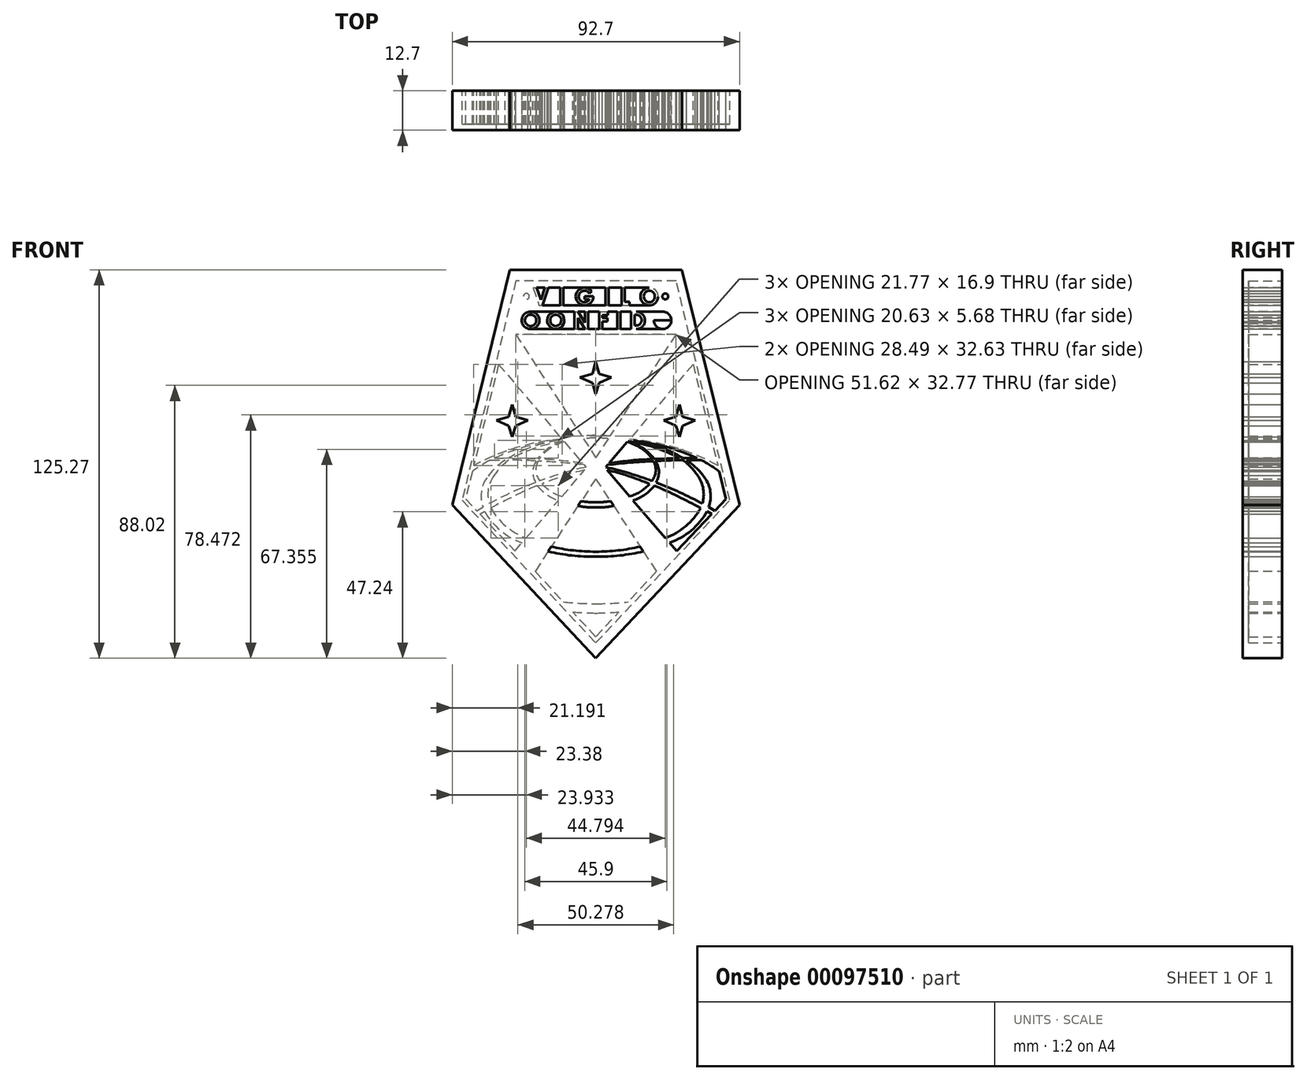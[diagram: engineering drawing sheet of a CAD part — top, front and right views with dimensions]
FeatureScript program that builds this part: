
annotation { "Feature Type Name" : "Feature", "Feature Type Description" : "" }
export const myFeature = defineFeature(function(context is Context, id is Id, definition is map)
    precondition{}
    {
        {
            var Q0;
            Q0=qCreatedBy(makeId("Front.planeOp"),FACE);
            var sketch = newSketch(context, id + "F0", { "sketchPlane" : qUnion([Q0])});
            skLineSegment(sketch, "E0", {"start": v(-27.72, 63.66) * mm, "end": v(27.8, 63.66) * mm});
            skLineSegment(sketch, "E1", {"start": v(27.8, 63.66) * mm, "end": v(46.37, -12.24) * mm});
            skLineSegment(sketch, "E2", {"start": v(46.37, -12.24) * mm, "end": v(0, -61.61) * mm});
            skLineSegment(sketch, "E3", {"start": v(0, -61.61) * mm, "end": v(-46.33, -12.22) * mm});
            skLineSegment(sketch, "E4", {"start": v(-46.33, -12.22) * mm, "end": v(-27.72, 63.66) * mm});
            skLineSegment(sketch, "E5", {"start": v(0, -56.69) * mm, "end": v(43.22, -10.66) * mm});
            skLineSegment(sketch, "E6", {"start": v(43.22, -10.66) * mm, "end": v(25.91, 60.08) * mm});
            skLineSegment(sketch, "E7", {"start": v(25.91, 60.08) * mm, "end": v(-25.8, 60.08) * mm});
            skLineSegment(sketch, "E8", {"start": v(-25.8, 60.08) * mm, "end": v(-43.16, -10.68) * mm});
            skLineSegment(sketch, "E9", {"start": v(-43.16, -10.68) * mm, "end": v(0, -56.69) * mm});
            skLineSegment(sketch, "E10", {"start": v(0, 42.8) * mm, "end": v(-25.81, 42.8) * mm});
            skLineSegment(sketch, "E11", {"start": v(-25.81, 42.8) * mm, "end": v(-4.52, 10.03) * mm});
            skArc(sketch, "E12", {"start": v(0, 10.25) * mm, "mid": v(-2.26, 10.2) * mm, "end": v(-4.52, 10.03) * mm});
            skArc(sketch, "E13", {"start": v(0, 9.4) * mm, "mid": v(-2, 9.35) * mm, "end": v(-3.98, 9.2) * mm});
            skLineSegment(sketch, "E14", {"start": v(-3.98, 9.2) * mm, "end": v(0, 3.07) * mm});
            skLineSegment(sketch, "E15", {"start": v(-31.38, 33.18) * mm, "end": v(-39.38, 0.55) * mm});
            skLineSegment(sketch, "E16", {"start": v(-39.38, 0.55) * mm, "end": v(-42.02, -10.21) * mm});
            skLineSegment(sketch, "E17", {"start": v(-42.02, -10.21) * mm, "end": v(-38.44, -14.03) * mm});
            skLineSegment(sketch, "E18", {"start": v(-38.44, -14.03) * mm, "end": v(-36.41, -12.8) * mm});
            skLineSegment(sketch, "E19", {"start": v(0, -3.74) * mm, "end": v(-4.71, -10.93) * mm});
            skArc(sketch, "E20", {"start": v(-4.71, -10.93) * mm, "mid": v(-2.37, -11.25) * mm, "end": v(0, -11.33) * mm});
            skLineSegment(sketch, "E21", {"start": v(-31.38, 33.18) * mm, "end": v(-10.9, 9.05) * mm});
            skArc(sketch, "E22", {"start": v(-10.9, 9.05) * mm, "mid": v(-25.59, 6.3) * mm, "end": v(-39.38, 0.55) * mm});
            skLineSegment(sketch, "E23", {"start": v(-4.71, -10.93) * mm, "end": v(-19.6, -33.58) * mm});
            skArc(sketch, "E24", {"start": v(-5.74, -12.49) * mm, "mid": v(-2.88, -12.9) * mm, "end": v(0, -12.98) * mm});
            skArc(sketch, "E25", {"start": v(-14.35, -25.6) * mm, "mid": v(-7.22, -26.85) * mm, "end": v(0, -27.25) * mm});
            skArc(sketch, "E26", {"start": v(-15.37, -27.15) * mm, "mid": v(-7.74, -28.5) * mm, "end": v(0, -28.86) * mm});
            skLineSegment(sketch, "E27", {"start": v(-19.6, -33.58) * mm, "end": v(-10.47, -43.42) * mm});
            skArc(sketch, "E28", {"start": v(-10.47, -43.42) * mm, "mid": v(-5.24, -43.89) * mm, "end": v(0, -44) * mm});
            skLineSegment(sketch, "E29", {"start": v(0, -54.67) * mm, "end": v(-7.47, -46.7) * mm});
            skArc(sketch, "E30", {"start": v(-7.47, -46.7) * mm, "mid": v(-3.74, -46.95) * mm, "end": v(0, -47.05) * mm});
            skLineSegment(sketch, "E31", {"start": v(-37.35, -15.14) * mm, "end": v(-26.15, -27.08) * mm});
            skLineSegment(sketch, "E32", {"start": v(-26.15, -27.08) * mm, "end": v(-3.6, -0.9) * mm});
            skLineSegment(sketch, "E33", {"start": v(-37.35, -15.14) * mm, "end": v(-35.92, -14.27) * mm});
            skArc(sketch, "E34", {"start": v(-35.92, -14.27) * mm, "mid": v(-30.77, -20.4) * mm, "end": v(-23.8, -24.36) * mm});
            skArc(sketch, "E35", {"start": v(-33.83, -13.18) * mm, "mid": v(-29, -19) * mm, "end": v(-22.48, -22.82) * mm});
            skArc(sketch, "E36", {"start": v(-18.92, -5.92) * mm, "mid": v(-26.46, -9.38) * mm, "end": v(-33.83, -13.18) * mm});
            skArc(sketch, "E37", {"start": v(-18.92, -5.92) * mm, "mid": v(-15.85, -8.84) * mm, "end": v(-12.07, -10.73) * mm});
            skArc(sketch, "E38", {"start": v(-17.38, -5.41) * mm, "mid": v(-14.42, -7.83) * mm, "end": v(-10.96, -9.45) * mm});
            skArc(sketch, "E39", {"start": v(-3.6, -0.9) * mm, "mid": v(-10.58, -2.87) * mm, "end": v(-17.38, -5.41) * mm});
            skArc(sketch, "E40", {"start": v(-35.16, -3.42) * mm, "mid": v(-36.94, -7.95) * mm, "end": v(-36.41, -12.8) * mm});
            skArc(sketch, "E41", {"start": v(-29.26, 2.3) * mm, "mid": v(-32.47, -0.3) * mm, "end": v(-35.16, -3.42) * mm});
            skArc(sketch, "E42", {"start": v(-34.08, 2.3) * mm, "mid": v(-37.02, 0.55) * mm, "end": v(-39.85, -1.36) * mm});
            skLineSegment(sketch, "E43", {"start": v(-34.08, 2.3) * mm, "end": v(-29.26, 2.3) * mm});
            skArc(sketch, "E44", {"start": v(-19.45, -4.9) * mm, "mid": v(-27.02, -8.1) * mm, "end": v(-34.4, -11.72) * mm});
            skArc(sketch, "E45", {"start": v(-3.2, 0) * mm, "mid": v(-10.74, -1.94) * mm, "end": v(-18.12, -4.43) * mm});
            skArc(sketch, "E46", {"start": v(-18.7, 1.96) * mm, "mid": v(-19.32, -1.32) * mm, "end": v(-18.12, -4.43) * mm});
            skArc(sketch, "E47", {"start": v(-32.86, -2.67) * mm, "mid": v(-34.67, -7.02) * mm, "end": v(-34.4, -11.72) * mm});
            skArc(sketch, "E48", {"start": v(-28.11, 2.3) * mm, "mid": v(-30.69, 0) * mm, "end": v(-32.86, -2.67) * mm});
            skArc(sketch, "E49", {"start": v(-19.27, 1.97) * mm, "mid": v(-23.69, 2.2) * mm, "end": v(-28.11, 2.3) * mm});
            skArc(sketch, "E50", {"start": v(-19.27, 1.97) * mm, "mid": v(-20.35, -1.44) * mm, "end": v(-19.45, -4.9) * mm});
            skArc(sketch, "E51", {"start": v(-3.77, 0.73) * mm, "mid": v(-11.22, 1.5) * mm, "end": v(-18.7, 1.96) * mm});
            skLineSegment(sketch, "E52", {"start": v(-3.77, 0.73) * mm, "end": v(-3.2, 0) * mm});
            skArc(sketch, "E53", {"start": v(-12.08, 8.58) * mm, "mid": v(-22.62, 6.57) * mm, "end": v(-32.71, 2.94) * mm});
            skArc(sketch, "E54", {"start": v(-12.08, 8.58) * mm, "mid": v(-17.09, 7.52) * mm, "end": v(-21.97, 6) * mm});
            skArc(sketch, "E55", {"start": v(-21.97, 6) * mm, "mid": v(-25.12, 4.62) * mm, "end": v(-28.11, 2.9) * mm});
            skLineSegment(sketch, "E56", {"start": v(-32.71, 2.94) * mm, "end": v(-28.11, 2.9) * mm});
            skLineSegment(sketch, "E57", {"start": v(-27.03, 2.9) * mm, "end": v(-18.91, 2.62) * mm});
            skArc(sketch, "E58", {"start": v(-10.43, 8.4) * mm, "mid": v(-18.97, 6.36) * mm, "end": v(-27.03, 2.9) * mm});
            skArc(sketch, "E59", {"start": v(-10.43, 8.4) * mm, "mid": v(-15.12, 6.17) * mm, "end": v(-18.91, 2.62) * mm});
            skArc(sketch, "E60", {"start": v(-4.3, 1.24) * mm, "mid": v(-11.3, 2.15) * mm, "end": v(-18.33, 2.58) * mm});
            skArc(sketch, "E61", {"start": v(-10.15, 8.17) * mm, "mid": v(-14.7, 6.06) * mm, "end": v(-18.33, 2.58) * mm});
            skLineSegment(sketch, "E62", {"start": v(-10.15, 8.17) * mm, "end": v(-4.3, 1.24) * mm});
            skLineSegment(sketch, "E63", {"start": v(-26.95, 21.38) * mm, "end": v(-26.95, 9.07) * mm});
            skLineSegment(sketch, "E64", {"start": v(-33.32, 15.14) * mm, "end": v(-20.5, 15.14) * mm});
            skPoint(sketch, "E65", {"position": v(-26.95, 15.14) * mm});
            skPoint(sketch, "E66", {"position": v(-26.95, 20.22) * mm});
            skPoint(sketch, "E67", {"position": v(-21.87, 15.14) * mm});
            skPoint(sketch, "E68", {"position": v(-26.95, 9.8) * mm});
            skPoint(sketch, "E69", {"position": v(-32.03, 15.14) * mm});
            skLineSegment(sketch, "E70", {"start": v(-26.95, 9.8) * mm, "end": v(-28.06, 13.3) * mm});
            skLineSegment(sketch, "E71", {"start": v(-28.06, 13.3) * mm, "end": v(-32.03, 15.14) * mm});
            skLineSegment(sketch, "E72", {"start": v(-32.03, 15.14) * mm, "end": v(-28.06, 16.24) * mm});
            skLineSegment(sketch, "E73", {"start": v(-28.06, 16.24) * mm, "end": v(-26.95, 20.22) * mm});
            skLineSegment(sketch, "E74", {"start": v(-26.95, 20.22) * mm, "end": v(-25.85, 16.26) * mm});
            skLineSegment(sketch, "E75", {"start": v(-25.85, 16.26) * mm, "end": v(-21.87, 15.14) * mm});
            skLineSegment(sketch, "E76", {"start": v(-21.87, 15.14) * mm, "end": v(-25.85, 13.31) * mm});
            skLineSegment(sketch, "E77", {"start": v(-25.85, 13.31) * mm, "end": v(-26.95, 9.8) * mm});
            skLineSegment(sketch, "E78", {"start": v(-5.4, 28.93) * mm, "end": v(6.92, 28.93) * mm});
            skLineSegment(sketch, "E79", {"start": v(0, 35.2) * mm, "end": v(0, 22.48) * mm});
            skPoint(sketch, "E80", {"position": v(-5.08, 28.93) * mm});
            skPoint(sketch, "E81", {"position": v(0, 34) * mm});
            skPoint(sketch, "E82", {"position": v(0, 23.6) * mm});
            skLineSegment(sketch, "E83", {"start": v(-5.08, 28.93) * mm, "end": v(-1.1, 27.16) * mm});
            skLineSegment(sketch, "E84", {"start": v(-1.1, 27.16) * mm, "end": v(0, 23.6) * mm});
            skLineSegment(sketch, "E85", {"start": v(-5.08, 28.93) * mm, "end": v(-1.1, 30.07) * mm});
            skLineSegment(sketch, "E86", {"start": v(-1.1, 30.07) * mm, "end": v(0, 34) * mm});
            skLineSegment(sketch, "E87.MirrorCS", {"start": v(1.1, 30.07) * mm, "end": v(0, 34) * mm});
            skLineSegment(sketch, "E88.MirrorCS", {"start": v(5.08, 28.93) * mm, "end": v(1.1, 30.07) * mm});
            skLineSegment(sketch, "E89.MirrorCS", {"start": v(5.08, 28.93) * mm, "end": v(1.1, 27.16) * mm});
            skLineSegment(sketch, "E90.MirrorCS", {"start": v(1.1, 27.16) * mm, "end": v(0, 23.6) * mm});
            skLineSegment(sketch, "E91.MirrorCS", {"start": v(25.81, 42.8) * mm, "end": v(4.52, 10.03) * mm});
            skLineSegment(sketch, "E92.MirrorCS", {"start": v(0, 42.8) * mm, "end": v(25.81, 42.8) * mm});
            skLineSegment(sketch, "E93.MirrorCS", {"start": v(26.95, 20.22) * mm, "end": v(25.85, 16.26) * mm});
            skLineSegment(sketch, "E94.MirrorCS", {"start": v(28.06, 16.24) * mm, "end": v(26.95, 20.22) * mm});
            skLineSegment(sketch, "E95.MirrorCS", {"start": v(32.03, 15.14) * mm, "end": v(28.06, 16.24) * mm});
            skLineSegment(sketch, "E96.MirrorCS", {"start": v(28.06, 13.3) * mm, "end": v(32.03, 15.14) * mm});
            skLineSegment(sketch, "E97.MirrorCS", {"start": v(26.95, 9.8) * mm, "end": v(28.06, 13.3) * mm});
            skLineSegment(sketch, "E98.MirrorCS", {"start": v(25.85, 13.31) * mm, "end": v(26.95, 9.8) * mm});
            skLineSegment(sketch, "E99.MirrorCS", {"start": v(21.87, 15.14) * mm, "end": v(25.85, 13.31) * mm});
            skLineSegment(sketch, "E100.MirrorCS", {"start": v(25.85, 16.26) * mm, "end": v(21.87, 15.14) * mm});
            skLineSegment(sketch, "E101.MirrorCS", {"start": v(31.38, 33.18) * mm, "end": v(10.9, 9.05) * mm});
            skLineSegment(sketch, "E102.MirrorCS", {"start": v(31.38, 33.18) * mm, "end": v(39.38, 0.55) * mm});
            skArc(sketch, "E103.MirrorCS", {"start": v(10.9, 9.05) * mm, "mid": v(25.59, 6.3) * mm, "end": v(39.38, 0.55) * mm});
            skArc(sketch, "E104.MirrorCS", {"start": v(12.08, 8.58) * mm, "mid": v(22.62, 6.57) * mm, "end": v(32.71, 2.94) * mm});
            skArc(sketch, "E105.MirrorCS", {"start": v(10.43, 8.4) * mm, "mid": v(18.97, 6.36) * mm, "end": v(27.03, 2.9) * mm});
            skArc(sketch, "E106.MirrorCS", {"start": v(21.97, 6) * mm, "mid": v(25.12, 4.62) * mm, "end": v(28.11, 2.9) * mm});
            skArc(sketch, "E107.MirrorCS", {"start": v(12.08, 8.58) * mm, "mid": v(17.09, 7.52) * mm, "end": v(21.97, 6) * mm});
            skLineSegment(sketch, "E108.MirrorCS", {"start": v(32.71, 2.94) * mm, "end": v(28.11, 2.9) * mm});
            skArc(sketch, "E109.MirrorCS", {"start": v(29.26, 2.3) * mm, "mid": v(32.47, -0.3) * mm, "end": v(35.16, -3.42) * mm});
            skArc(sketch, "E110.MirrorCS", {"start": v(34.08, 2.3) * mm, "mid": v(37.02, 0.55) * mm, "end": v(39.85, -1.36) * mm});
            skLineSegment(sketch, "E111.MirrorCS", {"start": v(39.38, 0.55) * mm, "end": v(42.02, -10.21) * mm});
            skLineSegment(sketch, "E112.MirrorCS", {"start": v(42.02, -10.21) * mm, "end": v(38.44, -14.03) * mm});
            skLineSegment(sketch, "E113.MirrorCS", {"start": v(38.44, -14.03) * mm, "end": v(36.41, -12.8) * mm});
            skArc(sketch, "E114.MirrorCS", {"start": v(35.16, -3.42) * mm, "mid": v(36.94, -7.95) * mm, "end": v(36.41, -12.8) * mm});
            skArc(sketch, "E115.MirrorCS", {"start": v(32.86, -2.67) * mm, "mid": v(34.67, -7.02) * mm, "end": v(34.4, -11.72) * mm});
            skArc(sketch, "E116.MirrorCS", {"start": v(28.11, 2.3) * mm, "mid": v(30.69, 0) * mm, "end": v(32.86, -2.67) * mm});
            skArc(sketch, "E117.MirrorCS", {"start": v(19.27, 1.97) * mm, "mid": v(23.69, 2.2) * mm, "end": v(28.11, 2.3) * mm});
            skLineSegment(sketch, "E118.MirrorCS", {"start": v(27.03, 2.9) * mm, "end": v(18.91, 2.62) * mm});
            skArc(sketch, "E119.MirrorCS", {"start": v(10.43, 8.4) * mm, "mid": v(15.12, 6.17) * mm, "end": v(18.91, 2.62) * mm});
            skArc(sketch, "E120.MirrorCS", {"start": v(10.15, 8.17) * mm, "mid": v(14.7, 6.06) * mm, "end": v(18.33, 2.58) * mm});
            skArc(sketch, "E121.MirrorCS", {"start": v(4.3, 1.24) * mm, "mid": v(11.3, 2.15) * mm, "end": v(18.33, 2.58) * mm});
            skLineSegment(sketch, "E122.MirrorCS", {"start": v(10.15, 8.17) * mm, "end": v(4.3, 1.24) * mm});
            skArc(sketch, "E123.MirrorCS", {"start": v(3.77, 0.73) * mm, "mid": v(11.22, 1.5) * mm, "end": v(18.7, 1.96) * mm});
            skArc(sketch, "E124.MirrorCS", {"start": v(3.2, 0) * mm, "mid": v(10.74, -1.94) * mm, "end": v(18.12, -4.43) * mm});
            skArc(sketch, "E125.MirrorCS", {"start": v(18.7, 1.96) * mm, "mid": v(19.32, -1.32) * mm, "end": v(18.12, -4.43) * mm});
            skArc(sketch, "E126.MirrorCS", {"start": v(19.27, 1.97) * mm, "mid": v(20.35, -1.44) * mm, "end": v(19.45, -4.9) * mm});
            skArc(sketch, "E127.MirrorCS", {"start": v(19.45, -4.9) * mm, "mid": v(27.02, -8.1) * mm, "end": v(34.4, -11.72) * mm});
            skArc(sketch, "E128.MirrorCS", {"start": v(5.74, -12.49) * mm, "mid": v(2.88, -12.9) * mm, "end": v(0, -12.98) * mm});
            skArc(sketch, "E129.MirrorCS", {"start": v(4.71, -10.93) * mm, "mid": v(2.37, -11.25) * mm, "end": v(0, -11.33) * mm});
            skLineSegment(sketch, "E130.MirrorCS", {"start": v(0, -3.74) * mm, "end": v(4.71, -10.93) * mm});
            skArc(sketch, "E131.MirrorCS", {"start": v(14.35, -25.6) * mm, "mid": v(7.22, -26.85) * mm, "end": v(0, -27.25) * mm});
            skLineSegment(sketch, "E132.MirrorCS", {"start": v(4.71, -10.93) * mm, "end": v(19.6, -33.58) * mm});
            skArc(sketch, "E133.MirrorCS", {"start": v(15.37, -27.15) * mm, "mid": v(7.74, -28.5) * mm, "end": v(0, -28.86) * mm});
            skArc(sketch, "E134.MirrorCS", {"start": v(10.47, -43.42) * mm, "mid": v(5.24, -43.89) * mm, "end": v(0, -44) * mm});
            skLineSegment(sketch, "E135.MirrorCS", {"start": v(19.6, -33.58) * mm, "end": v(10.47, -43.42) * mm});
            skArc(sketch, "E136.MirrorCS", {"start": v(7.47, -46.7) * mm, "mid": v(3.74, -46.95) * mm, "end": v(0, -47.05) * mm});
            skLineSegment(sketch, "E137.MirrorCS", {"start": v(0, -54.67) * mm, "end": v(7.47, -46.7) * mm});
            skArc(sketch, "E138.MirrorCS", {"start": v(0, 9.4) * mm, "mid": v(2, 9.35) * mm, "end": v(3.98, 9.2) * mm});
            skLineSegment(sketch, "E139.MirrorCS", {"start": v(3.98, 9.2) * mm, "end": v(0, 3.07) * mm});
            skArc(sketch, "E140.MirrorCS", {"start": v(0, 10.25) * mm, "mid": v(2.26, 10.2) * mm, "end": v(4.52, 10.03) * mm});
            skLineSegment(sketch, "E141", {"start": v(-21, 57.88) * mm, "end": v(22.36, 57.88) * mm});
            skLineSegment(sketch, "E142", {"start": v(-20.05, 52.23) * mm, "end": v(23.28, 52.23) * mm});
            skLineSegment(sketch, "E143", {"start": v(-24.15, 50.19) * mm, "end": v(26.1, 50.19) * mm});
            skLineSegment(sketch, "E144", {"start": v(-24.97, 44.55) * mm, "end": v(26.4, 44.55) * mm});
            skLineSegment(sketch, "E145", {"start": v(-20.24, 57.88) * mm, "end": v(-18.3, 52.23) * mm});
            skLineSegment(sketch, "E146", {"start": v(-19.09, 57.88) * mm, "end": v(-17.76, 54.01) * mm});
            skLineSegment(sketch, "E147", {"start": v(-17.76, 54.01) * mm, "end": v(-16.44, 57.88) * mm});
            skLineSegment(sketch, "E148", {"start": v(-15.29, 57.88) * mm, "end": v(-17.2, 52.23) * mm});
            skLineSegment(sketch, "E149", {"start": v(-11.48, 57.88) * mm, "end": v(-11.48, 52.23) * mm});
            skLineSegment(sketch, "E150", {"start": v(-10.43, 57.88) * mm, "end": v(-10.43, 52.23) * mm});
            skLineSegment(sketch, "E151", {"start": v(3.05, 57.88) * mm, "end": v(3.05, 52.23) * mm});
            skLineSegment(sketch, "E152", {"start": v(4.15, 57.88) * mm, "end": v(4.15, 52.23) * mm});
            skLineSegment(sketch, "E153", {"start": v(8.3, 57.88) * mm, "end": v(8.3, 52.23) * mm});
            skLineSegment(sketch, "E154", {"start": v(10.92, 52.23) * mm, "end": v(10.92, 53.33) * mm});
            skLineSegment(sketch, "E155", {"start": v(10.92, 53.33) * mm, "end": v(9.39, 53.33) * mm});
            skLineSegment(sketch, "E156", {"start": v(9.39, 53.33) * mm, "end": v(9.39, 57.88) * mm});
            skLineSegment(sketch, "E157", {"start": v(-23.92, 55.08) * mm, "end": v(-20.8, 55.08) * mm});
            skLineSegment(sketch, "E158", {"start": v(-22.42, 54.08) * mm, "end": v(-22.42, 56.2) * mm});
            skCircle(sketch, "E159", {"center": v(-22.42, 55.08) * mm, "radius": 0.95 * mm});
            skCircle(sketch, "E160.MirrorC", {"center": v(22.42, 55.08) * mm, "radius": 0.95 * mm});
            skLineSegment(sketch, "E161", {"start": v(1.04, 50.19) * mm, "end": v(1.04, 44.55) * mm});
            skLineSegment(sketch, "E162", {"start": v(3.87, 50.19) * mm, "end": v(3.87, 49.1) * mm});
            skLineSegment(sketch, "E163", {"start": v(3.87, 49.1) * mm, "end": v(2.13, 49.1) * mm});
            skLineSegment(sketch, "E164", {"start": v(2.13, 49.1) * mm, "end": v(2.13, 48.15) * mm});
            skLineSegment(sketch, "E165", {"start": v(2.13, 48.15) * mm, "end": v(3.74, 48.15) * mm});
            skLineSegment(sketch, "E166", {"start": v(3.74, 48.15) * mm, "end": v(3.74, 47.06) * mm});
            skLineSegment(sketch, "E167", {"start": v(3.74, 47.06) * mm, "end": v(2.13, 47.06) * mm});
            skLineSegment(sketch, "E168", {"start": v(2.13, 47.06) * mm, "end": v(2.13, 44.55) * mm});
            skLineSegment(sketch, "E169", {"start": v(6.88, 50.19) * mm, "end": v(6.88, 44.55) * mm});
            skLineSegment(sketch, "E170", {"start": v(7.98, 50.19) * mm, "end": v(7.98, 44.55) * mm});
            skLineSegment(sketch, "E171", {"start": v(11.37, 50.19) * mm, "end": v(11.37, 44.55) * mm});
            skLineSegment(sketch, "E172", {"start": v(-6.9, 50.19) * mm, "end": v(-6.9, 44.55) * mm});
            skLineSegment(sketch, "E173", {"start": v(-2.44, 50.19) * mm, "end": v(-2.44, 44.55) * mm});
            skLineSegment(sketch, "E174", {"start": v(-3.53, 50.19) * mm, "end": v(-3.53, 46.59) * mm});
            skLineSegment(sketch, "E175", {"start": v(-3.53, 46.59) * mm, "end": v(-5.8, 50.19) * mm});
            skLineSegment(sketch, "E176", {"start": v(-5.8, 44.55) * mm, "end": v(-5.8, 48.14) * mm});
            skLineSegment(sketch, "E177", {"start": v(-5.8, 48.14) * mm, "end": v(-3.53, 44.55) * mm});
            skLineSegment(sketch, "E178", {"start": v(21.54, 50.19) * mm, "end": v(21.54, 44.55) * mm});
            skLineSegment(sketch, "E179", {"start": v(17.82, 47.41) * mm, "end": v(25.25, 47.41) * mm});
            skEllipse(sketch, "E180", {"center": v(21.54, 47.37) * mm, "majorRadius": 2.82 * mm, "minorRadius": 2.81 * mm, "majorAxis": v(0, -1)});
            skEllipse(sketch, "E181", {"center": v(21.54, 47.37) * mm, "majorRadius": 1.85 * mm, "minorRadius": 1.8 * mm, "majorAxis": v(0, -1)});
            skLineSegment(sketch, "E182", {"start": v(17.26, 57.88) * mm, "end": v(17.26, 52.23) * mm});
            skLineSegment(sketch, "E183", {"start": v(13.99, 55.05) * mm, "end": v(20.7, 55.05) * mm});
            skPoint(sketch, "E183.startSnap0", {"position": v(17.26, 55.05) * mm});
            skEllipse(sketch, "E184", {"center": v(17.26, 55.05) * mm, "majorRadius": 2.82 * mm, "minorRadius": 2.87 * mm, "majorAxis": v(0, -1)});
            skEllipse(sketch, "E185", {"center": v(17.26, 55.05) * mm, "majorRadius": 1.84 * mm, "minorRadius": 1.78 * mm, "majorAxis": v(0, -1)});
            skLineSegment(sketch, "E186", {"start": v(-12.94, 50.19) * mm, "end": v(-12.94, 44.55) * mm});
            skEllipse(sketch, "E187", {"center": v(-12.94, 47.37) * mm, "majorRadius": 2.82 * mm, "minorRadius": 2.8 * mm, "majorAxis": v(0, -1)});
            skEllipse(sketch, "E188", {"center": v(-12.94, 47.37) * mm, "majorRadius": 1.83 * mm, "minorRadius": 1.78 * mm, "majorAxis": v(0, -1)});
            skLineSegment(sketch, "E189", {"start": v(-21.03, 50.19) * mm, "end": v(-21.03, 44.55) * mm});
            skEllipse(sketch, "E190", {"center": v(-21.03, 47.37) * mm, "majorRadius": 2.82 * mm, "minorRadius": 2.88 * mm, "majorAxis": v(0, -1)});
            skEllipse(sketch, "E191", {"center": v(-21.03, 47.37) * mm, "majorRadius": 1.85 * mm, "minorRadius": 1.85 * mm, "majorAxis": v(0, -1)});
            skLineSegment(sketch, "E192", {"start": v(-18.75, 49.08) * mm, "end": v(-22.09, 45.84) * mm});
            skLineSegment(sketch, "E193", {"start": v(-18.74, 45.66) * mm, "end": v(-19.45, 46.4) * mm});
            skLineSegment(sketch, "E194", {"start": v(11.37, 50.19) * mm, "end": v(13.06, 50.19) * mm});
            skArc(sketch, "E195", {"start": v(13.06, 50.19) * mm, "mid": v(15.88, 47.37) * mm, "end": v(13.06, 44.55) * mm});
            skLineSegment(sketch, "E196", {"start": v(12.46, 49.14) * mm, "end": v(12.46, 45.7) * mm});
            skLineSegment(sketch, "E197", {"start": v(12.46, 49.14) * mm, "end": v(13.06, 49.14) * mm});
            skLineSegment(sketch, "E198", {"start": v(12.46, 45.7) * mm, "end": v(13.06, 45.7) * mm});
            skArc(sketch, "E199", {"start": v(13.06, 45.7) * mm, "mid": v(14.77, 47.42) * mm, "end": v(13.06, 49.14) * mm});
            skLineSegment(sketch, "E200", {"start": v(-3.64, 57.88) * mm, "end": v(-3.64, 52.23) * mm});
            skEllipse(sketch, "E201", {"center": v(-3.64, 55.05) * mm, "majorRadius": 2.82 * mm, "minorRadius": 2.86 * mm, "majorAxis": v(0, -1)});
            skEllipse(sketch, "E202", {"center": v(-3.64, 55.05) * mm, "majorRadius": 1.85 * mm, "minorRadius": 1.85 * mm, "majorAxis": v(0, -1)});
            skLineSegment(sketch, "E203", {"start": v(-4.7, 53.53) * mm, "end": v(-1.38, 56.78) * mm});
            skLineSegment(sketch, "E204", {"start": v(-0.78, 55.13) * mm, "end": v(-3.64, 55.13) * mm});
            skLineSegment(sketch, "E205", {"start": v(-3.64, 55.13) * mm, "end": v(-3.64, 54.12) * mm});
            skLineSegment(sketch, "E206", {"start": v(-3.64, 54.12) * mm, "end": v(-2.04, 54.12) * mm});
            skLineSegment(sketch, "E207", {"start": v(2.13, 47.06) * mm, "end": v(2.13, 48.15) * mm});
            skLineSegment(sketch, "E208.MirrorCS", {"start": v(26.15, -27.08) * mm, "end": v(3.6, -0.9) * mm});
            skArc(sketch, "E209.MirrorCS", {"start": v(3.6, -0.9) * mm, "mid": v(10.58, -2.87) * mm, "end": v(17.38, -5.41) * mm});
            skArc(sketch, "E210.MirrorCS", {"start": v(17.38, -5.41) * mm, "mid": v(14.42, -7.83) * mm, "end": v(10.96, -9.45) * mm});
            skArc(sketch, "E211.MirrorCS", {"start": v(18.92, -5.92) * mm, "mid": v(15.85, -8.84) * mm, "end": v(12.07, -10.73) * mm});
            skArc(sketch, "E212.MirrorCS", {"start": v(18.92, -5.92) * mm, "mid": v(26.46, -9.38) * mm, "end": v(33.83, -13.18) * mm});
            skArc(sketch, "E213.MirrorCS", {"start": v(33.83, -13.18) * mm, "mid": v(29, -19) * mm, "end": v(22.48, -22.82) * mm});
            skArc(sketch, "E214.MirrorCS", {"start": v(35.92, -14.27) * mm, "mid": v(30.77, -20.4) * mm, "end": v(23.8, -24.36) * mm});
            skLineSegment(sketch, "E215.MirrorCS", {"start": v(37.35, -15.14) * mm, "end": v(26.15, -27.08) * mm});
            skLineSegment(sketch, "E216.MirrorCS", {"start": v(37.35, -15.14) * mm, "end": v(35.92, -14.27) * mm});
            skLineSegment(sketch, "E217", {"start": v(3.77, 0.73) * mm, "end": v(3.2, 0) * mm});
            skLineSegment(sketch, "E218.MirrorCS", {"start": v(34.08, 2.3) * mm, "end": v(29.26, 2.3) * mm});
            skSolve(sketch);
        }
        {
            var Q0;
            Q0=makeQuery(id+"F0.imprint","IMPRINT",FACE,{"disambiguationData":[TD([[makeQuery(id+"F0.imprint","IMPRINT",EDGE,{"derivedFrom":sQuery(id+"F0.wireOp",EDGE,"E0")}),-1.0]])]});
            var Q1;
            Q1=makeQuery(id+"F0.imprint","IMPRINT",FACE,{"disambiguationData":[TD([[makeQuery(id+"F0.imprint","IMPRINT",EDGE,{"derivedFrom":sQuery(id+"F0.wireOp",EDGE,"E15")}),1.0]])]});
            var Q2;
            Q2=makeQuery(id+"F0.imprint","IMPRINT",FACE,{"disambiguationData":[TD([[makeQuery(id+"F0.imprint","IMPRINT",EDGE,{"derivedFrom":sQuery(id+"F0.wireOp",EDGE,"E53")}),1.0]])]});
            var Q3;
            {var subQ0=sQuery(id+"F0.wireOp",EDGE,"E17");Q3=makeQuery(id+"F0.imprint","IMPRINT",FACE,{"disambiguationData":[TD([[makeQuery(id+"F0.imprint","IMPRINT",EDGE,{"derivedFrom":subQ0}),1.0]])]});}
            var Q4;
            Q4=makeQuery(id+"F0.imprint","IMPRINT",FACE,{"disambiguationData":[TD([[makeQuery(id+"F0.imprint","IMPRINT",EDGE,{"derivedFrom":sQuery(id+"F0.wireOp",EDGE,"E44")}),-1.0]])]});
            var Q5;
            Q5=makeQuery(id+"F0.imprint","IMPRINT",FACE,{"disambiguationData":[TD([[makeQuery(id+"F0.imprint","IMPRINT",EDGE,{"derivedFrom":sQuery(id+"F0.wireOp",EDGE,"E57")}),1.0]])]});
            var Q6;
            Q6=makeQuery(id+"F0.imprint","IMPRINT",FACE,{"disambiguationData":[TD([[makeQuery(id+"F0.imprint","IMPRINT",EDGE,{"derivedFrom":sQuery(id+"F0.wireOp",EDGE,"E60")}),-1.0]])]});
            var Q7;
            Q7=makeQuery(id+"F0.imprint","IMPRINT",FACE,{"disambiguationData":[TD([[makeQuery(id+"F0.imprint","IMPRINT",EDGE,{"derivedFrom":sQuery(id+"F0.wireOp",EDGE,"E45")}),-1.0]])]});
            var Q8;
            {var subQ2=sQuery(id+"F0.wireOp",EDGE,"E38");Q8=makeQuery(id+"F0.imprint","IMPRINT",FACE,{"disambiguationData":[TD([[makeQuery(id+"F0.imprint","IMPRINT",EDGE,{"derivedFrom":subQ2}),1.0]])]});}
            var Q9;
            {var subQ0=sQuery(id+"F0.wireOp",EDGE,"E35");Q9=makeQuery(id+"F0.imprint","IMPRINT",FACE,{"disambiguationData":[TD([[makeQuery(id+"F0.imprint","IMPRINT",EDGE,{"derivedFrom":subQ0}),1.0]])]});}
            var Q10;
            {var subQ0=sQuery(id+"F0.wireOp",EDGE,"E31");Q10=makeQuery(id+"F0.imprint","IMPRINT",FACE,{"disambiguationData":[TD([[makeQuery(id+"F0.imprint","IMPRINT",EDGE,{"derivedFrom":subQ0}),1.0]])]});}
            var Q11;
            {var subQ1=sQuery(id+"F0.wireOp",EDGE,"E24");Q11=makeQuery(id+"F0.imprint","IMPRINT",FACE,{"disambiguationData":[TD([[makeQuery(id+"F0.imprint","IMPRINT",EDGE,{"derivedFrom":subQ1}),-1.0]])]});}
            var Q12;
            Q12=makeQuery(id+"F0.imprint","IMPRINT",FACE,{"disambiguationData":[TD([[makeQuery(id+"F0.imprint","IMPRINT",EDGE,{"derivedFrom":sQuery(id+"F0.wireOp",EDGE,"E19")}),1.0]])]});
            var Q13;
            {var subQ1=sQuery(id+"F0.wireOp",EDGE,"E26");Q13=makeQuery(id+"F0.imprint","IMPRINT",FACE,{"disambiguationData":[TD([[makeQuery(id+"F0.imprint","IMPRINT",EDGE,{"derivedFrom":subQ1}),-1.0]])]});}
            var Q14;
            Q14=makeQuery(id+"F0.imprint","IMPRINT",FACE,{"disambiguationData":[TD([[makeQuery(id+"F0.imprint","IMPRINT",EDGE,{"derivedFrom":sQuery(id+"F0.wireOp",EDGE,"E29")}),-1.0]])]});
            var Q15;
            Q15=makeQuery(id+"F0.imprint","IMPRINT",FACE,{"disambiguationData":[TD([[makeQuery(id+"F0.imprint","IMPRINT",EDGE,{"derivedFrom":sQuery(id+"F0.wireOp",EDGE,"E13")}),1.0]])]});
            var Q16;
            Q16=makeQuery(id+"F0.imprint","IMPRINT",FACE,{"disambiguationData":[TD([[makeQuery(id+"F0.imprint","IMPRINT",EDGE,{"derivedFrom":sQuery(id+"F0.wireOp",EDGE,"E120.MirrorCS")}),-1.0]])]});
            var Q17;
            Q17=makeQuery(id+"F0.imprint","IMPRINT",FACE,{"disambiguationData":[TD([[makeQuery(id+"F0.imprint","IMPRINT",EDGE,{"derivedFrom":sQuery(id+"F0.wireOp",EDGE,"E115.MirrorCS")}),-1.0]])]});
            var Q18;
            Q18=makeQuery(id+"F0.imprint","IMPRINT",FACE,{"disambiguationData":[TD([[makeQuery(id+"F0.imprint","IMPRINT",EDGE,{"derivedFrom":sQuery(id+"F0.wireOp",EDGE,"E93.MirrorCS")}),-1.0]])]});
            var Q19;
            Q19=makeQuery(id+"F0.imprint","IMPRINT",FACE,{"disambiguationData":[TD([[makeQuery(id+"F0.imprint","IMPRINT",EDGE,{"derivedFrom":sQuery(id+"F0.wireOp",EDGE,"E104.MirrorCS")}),-1.0]])]});
            var Q20;
            Q20=makeQuery(id+"F0.imprint","IMPRINT",FACE,{"disambiguationData":[TD([[makeQuery(id+"F0.imprint","IMPRINT",EDGE,{"derivedFrom":sQuery(id+"F0.wireOp",EDGE,"E105.MirrorCS")}),-1.0]])]});
            var Q21;
            Q21=makeQuery(id+"F0.imprint","IMPRINT",FACE,{"disambiguationData":[TD([[makeQuery(id+"F0.imprint","IMPRINT",EDGE,{"derivedFrom":sQuery(id+"F0.wireOp",EDGE,"E10")}),1.0]])]});
            var Q22;
            {var subQ0=sQuery(id+"F0.wireOp",EDGE,"E145");Q22=makeQuery(id+"F0.imprint","IMPRINT",FACE,{"disambiguationData":[TD([[makeQuery(id+"F0.imprint","IMPRINT",EDGE,{"derivedFrom":subQ0}),1.0]])]});}
            var Q23;
            {var subQ0=sQuery(id+"F0.wireOp",EDGE,"E159");var subQ1=sQuery(id+"F0.wireOp",EDGE,"E157");var subQ2=makeQuery(id+"F0.imprint","INTERSECT",VERTEX,{"disambiguationData":[OD(1.0)],"derivedFrom":[subQ1,subQ0]});Q23=makeQuery(id+"F0.imprint","IMPRINT",FACE,{"disambiguationData":[TD([[makeQuery(id+"F0.imprint","IMPRINT",EDGE,{"disambiguationData":[TD([[subQ2,1.0]])],"derivedFrom":subQ1}),1.0]])]});}
            var Q24;
            {var subQ0=sQuery(id+"F0.wireOp",EDGE,"E159");var subQ1=sQuery(id+"F0.wireOp",EDGE,"E157");var subQ2=makeQuery(id+"F0.imprint","INTERSECT",VERTEX,{"disambiguationData":[OD(1.0)],"derivedFrom":[subQ1,subQ0]});Q24=makeQuery(id+"F0.imprint","IMPRINT",FACE,{"disambiguationData":[TD([[makeQuery(id+"F0.imprint","IMPRINT",EDGE,{"disambiguationData":[TD([[subQ2,1.0]])],"derivedFrom":subQ1}),-1.0]])]});}
            var Q25;
            {var subQ0=sQuery(id+"F0.wireOp",EDGE,"E159");var subQ1=sQuery(id+"F0.wireOp",EDGE,"E157");var subQ2=makeQuery(id+"F0.imprint","INTERSECT",VERTEX,{"disambiguationData":[OD(0.0)],"derivedFrom":[subQ1,subQ0]});Q25=makeQuery(id+"F0.imprint","IMPRINT",FACE,{"disambiguationData":[TD([[makeQuery(id+"F0.imprint","IMPRINT",EDGE,{"disambiguationData":[TD([[subQ2,-1.0]])],"derivedFrom":subQ1}),-1.0]])]});}
            var Q26;
            {var subQ0=sQuery(id+"F0.wireOp",EDGE,"E159");var subQ1=sQuery(id+"F0.wireOp",EDGE,"E157");var subQ2=makeQuery(id+"F0.imprint","INTERSECT",VERTEX,{"disambiguationData":[OD(0.0)],"derivedFrom":[subQ1,subQ0]});Q26=makeQuery(id+"F0.imprint","IMPRINT",FACE,{"disambiguationData":[TD([[makeQuery(id+"F0.imprint","IMPRINT",EDGE,{"disambiguationData":[TD([[subQ2,-1.0]])],"derivedFrom":subQ1}),1.0]])]});}
            var Q27;
            {var subQ0=sQuery(id+"F0.wireOp",EDGE,"E191");var subQ1=makeQuery(id+"F0.imprint","INTERSECT",VERTEX,{"disambiguationData":[OD(0.0)],"derivedFrom":[subQ0,sQuery(id+"F0.wireOp",EDGE,"E192")]});Q27=makeQuery(id+"F0.imprint","IMPRINT",FACE,{"disambiguationData":[TD([[makeQuery(id+"F0.imprint","IMPRINT",EDGE,{"disambiguationData":[TD([[subQ1,1.0]])],"derivedFrom":subQ0}),-1.0]])]});}
            var Q28;
            {var subQ1=sQuery(id+"F0.wireOp",EDGE,"E189");var subQ3=sQuery(id+"F0.wireOp",EDGE,"E191");var subQ4=makeQuery(id+"F0.imprint","INTERSECT",VERTEX,{"disambiguationData":[OD(0.0)],"derivedFrom":[subQ1,subQ3]});Q28=makeQuery(id+"F0.imprint","IMPRINT",FACE,{"disambiguationData":[TD([[makeQuery(id+"F0.imprint","IMPRINT",EDGE,{"disambiguationData":[TD([[subQ4,1.0]])],"derivedFrom":subQ3}),-1.0]])]});}
            var Q29;
            {var subQ5=sQuery(id+"F0.wireOp",EDGE,"E193");Q29=makeQuery(id+"F0.imprint","IMPRINT",FACE,{"disambiguationData":[TD([[makeQuery(id+"F0.imprint","IMPRINT",EDGE,{"derivedFrom":subQ5}),1.0]])]});}
            var Q30;
            {var subQ1=sQuery(id+"F0.wireOp",EDGE,"E186");var subQ3=sQuery(id+"F0.wireOp",EDGE,"E188");var subQ4=makeQuery(id+"F0.imprint","INTERSECT",VERTEX,{"disambiguationData":[OD(0.0)],"derivedFrom":[subQ1,subQ3]});Q30=makeQuery(id+"F0.imprint","IMPRINT",FACE,{"disambiguationData":[TD([[makeQuery(id+"F0.imprint","IMPRINT",EDGE,{"disambiguationData":[TD([[subQ4,-1.0]])],"derivedFrom":subQ3}),-1.0]])]});}
            var Q31;
            {var subQ1=sQuery(id+"F0.wireOp",EDGE,"E186");var subQ3=sQuery(id+"F0.wireOp",EDGE,"E188");var subQ4=makeQuery(id+"F0.imprint","INTERSECT",VERTEX,{"disambiguationData":[OD(0.0)],"derivedFrom":[subQ1,subQ3]});Q31=makeQuery(id+"F0.imprint","IMPRINT",FACE,{"disambiguationData":[TD([[makeQuery(id+"F0.imprint","IMPRINT",EDGE,{"disambiguationData":[TD([[subQ4,1.0]])],"derivedFrom":subQ3}),-1.0]])]});}
            var Q32;
            {var subQ0=sQuery(id+"F0.wireOp",EDGE,"E149");Q32=makeQuery(id+"F0.imprint","IMPRINT",FACE,{"disambiguationData":[TD([[makeQuery(id+"F0.imprint","IMPRINT",EDGE,{"derivedFrom":subQ0}),1.0]])]});}
            var Q33;
            {var subQ4=sQuery(id+"F0.wireOp",EDGE,"E202");var subQ5=makeQuery(id+"F0.imprint","INTERSECT",VERTEX,{"disambiguationData":[OD(0.0)],"derivedFrom":[subQ4,sQuery(id+"F0.wireOp",EDGE,"E203")]});Q33=makeQuery(id+"F0.imprint","IMPRINT",FACE,{"disambiguationData":[TD([[makeQuery(id+"F0.imprint","IMPRINT",EDGE,{"disambiguationData":[TD([[subQ5,1.0]])],"derivedFrom":subQ4}),-1.0]])]});}
            var Q34;
            {var subQ1=sQuery(id+"F0.wireOp",EDGE,"E200");var subQ3=sQuery(id+"F0.wireOp",EDGE,"E202");var subQ4=makeQuery(id+"F0.imprint","INTERSECT",VERTEX,{"disambiguationData":[OD(0.0)],"derivedFrom":[subQ1,subQ3]});Q34=makeQuery(id+"F0.imprint","IMPRINT",FACE,{"disambiguationData":[TD([[makeQuery(id+"F0.imprint","IMPRINT",EDGE,{"disambiguationData":[TD([[subQ4,1.0]])],"derivedFrom":subQ3}),-1.0]])]});}
            var Q35;
            {var subQ0=sQuery(id+"F0.wireOp",EDGE,"E202");var subQ1=makeQuery(id+"F0.imprint","INTERSECT",VERTEX,{"derivedFrom":[subQ0,sQuery(id+"F0.wireOp",EDGE,"E206")]});Q35=makeQuery(id+"F0.imprint","IMPRINT",FACE,{"disambiguationData":[TD([[makeQuery(id+"F0.imprint","IMPRINT",EDGE,{"disambiguationData":[TD([[subQ1,1.0]])],"derivedFrom":subQ0}),-1.0]])]});}
            var Q36;
            {var subQ0=sQuery(id+"F0.wireOp",EDGE,"E206");Q36=makeQuery(id+"F0.imprint","IMPRINT",FACE,{"disambiguationData":[TD([[makeQuery(id+"F0.imprint","IMPRINT",EDGE,{"derivedFrom":subQ0}),1.0]])]});}
            var Q37;
            {var subQ0=sQuery(id+"F0.wireOp",EDGE,"E205");var subQ1=sQuery(id+"F0.wireOp",EDGE,"E203");var subQ2=makeQuery(id+"F0.imprint","INTERSECT",VERTEX,{"derivedFrom":[subQ1,subQ0]});Q37=makeQuery(id+"F0.imprint","IMPRINT",FACE,{"disambiguationData":[TD([[makeQuery(id+"F0.imprint","IMPRINT",EDGE,{"disambiguationData":[TD([[subQ2,-1.0]])],"derivedFrom":subQ1}),1.0]])]});}
            var Q38;
            {var subQ0=sQuery(id+"F0.wireOp",EDGE,"E151");Q38=makeQuery(id+"F0.imprint","IMPRINT",FACE,{"disambiguationData":[TD([[makeQuery(id+"F0.imprint","IMPRINT",EDGE,{"derivedFrom":subQ0}),1.0]])]});}
            var Q39;
            {var subQ1=sQuery(id+"F0.wireOp",EDGE,"E161");Q39=makeQuery(id+"F0.imprint","IMPRINT",FACE,{"disambiguationData":[TD([[makeQuery(id+"F0.imprint","IMPRINT",EDGE,{"derivedFrom":subQ1}),1.0]])]});}
            var Q40;
            Q40=makeQuery(id+"F0.imprint","IMPRINT",FACE,{"disambiguationData":[TD([[makeQuery(id+"F0.imprint","IMPRINT",EDGE,{"derivedFrom":sQuery(id+"F0.wireOp",EDGE,"E165")}),-1.0]])]});
            var Q41;
            {var subQ0=sQuery(id+"F0.wireOp",EDGE,"E172");Q41=makeQuery(id+"F0.imprint","IMPRINT",FACE,{"disambiguationData":[TD([[makeQuery(id+"F0.imprint","IMPRINT",EDGE,{"derivedFrom":subQ0}),1.0]])]});}
            var Q42;
            {var subQ1=sQuery(id+"F0.wireOp",EDGE,"E153");Q42=makeQuery(id+"F0.imprint","IMPRINT",FACE,{"disambiguationData":[TD([[makeQuery(id+"F0.imprint","IMPRINT",EDGE,{"derivedFrom":subQ1}),1.0]])]});}
            var Q43;
            {var subQ0=sQuery(id+"F0.wireOp",EDGE,"E169");Q43=makeQuery(id+"F0.imprint","IMPRINT",FACE,{"disambiguationData":[TD([[makeQuery(id+"F0.imprint","IMPRINT",EDGE,{"derivedFrom":subQ0}),1.0]])]});}
            var Q44;
            {var subQ1=sQuery(id+"F0.wireOp",EDGE,"E171");Q44=makeQuery(id+"F0.imprint","IMPRINT",FACE,{"disambiguationData":[TD([[makeQuery(id+"F0.imprint","IMPRINT",EDGE,{"derivedFrom":subQ1}),1.0]])]});}
            var Q45;
            {var subQ0=sQuery(id+"F0.wireOp",EDGE,"E184");var subQ5=sQuery(id+"F0.wireOp",EDGE,"E183");var subQ6=makeQuery(id+"F0.imprint","INTERSECT",VERTEX,{"disambiguationData":[OD(0.0)],"derivedFrom":[subQ5,subQ0]});Q45=makeQuery(id+"F0.imprint","IMPRINT",FACE,{"disambiguationData":[TD([[makeQuery(id+"F0.imprint","IMPRINT",EDGE,{"disambiguationData":[TD([[subQ6,-1.0]])],"derivedFrom":subQ5}),-1.0]])]});}
            var Q46;
            {var subQ0=sQuery(id+"F0.wireOp",EDGE,"E184");var subQ5=sQuery(id+"F0.wireOp",EDGE,"E183");var subQ6=makeQuery(id+"F0.imprint","INTERSECT",VERTEX,{"disambiguationData":[OD(0.0)],"derivedFrom":[subQ5,subQ0]});Q46=makeQuery(id+"F0.imprint","IMPRINT",FACE,{"disambiguationData":[TD([[makeQuery(id+"F0.imprint","IMPRINT",EDGE,{"disambiguationData":[TD([[subQ6,-1.0]])],"derivedFrom":subQ5}),1.0]])]});}
            var Q47;
            {var subQ0=sQuery(id+"F0.wireOp",EDGE,"E184");var subQ5=sQuery(id+"F0.wireOp",EDGE,"E183");var subQ6=makeQuery(id+"F0.imprint","INTERSECT",VERTEX,{"disambiguationData":[OD(1.0)],"derivedFrom":[subQ5,subQ0]});Q47=makeQuery(id+"F0.imprint","IMPRINT",FACE,{"disambiguationData":[TD([[makeQuery(id+"F0.imprint","IMPRINT",EDGE,{"disambiguationData":[TD([[subQ6,1.0]])],"derivedFrom":subQ5}),1.0]])]});}
            var Q48;
            {var subQ0=sQuery(id+"F0.wireOp",EDGE,"E184");var subQ5=sQuery(id+"F0.wireOp",EDGE,"E183");var subQ6=makeQuery(id+"F0.imprint","INTERSECT",VERTEX,{"disambiguationData":[OD(1.0)],"derivedFrom":[subQ5,subQ0]});Q48=makeQuery(id+"F0.imprint","IMPRINT",FACE,{"disambiguationData":[TD([[makeQuery(id+"F0.imprint","IMPRINT",EDGE,{"disambiguationData":[TD([[subQ6,1.0]])],"derivedFrom":subQ5}),-1.0]])]});}
            var Q49;
            {var subQ0=sQuery(id+"F0.wireOp",EDGE,"E180");var subQ5=sQuery(id+"F0.wireOp",EDGE,"E179");var subQ6=makeQuery(id+"F0.imprint","INTERSECT",VERTEX,{"disambiguationData":[OD(0.0)],"derivedFrom":[subQ5,subQ0]});Q49=makeQuery(id+"F0.imprint","IMPRINT",FACE,{"disambiguationData":[TD([[makeQuery(id+"F0.imprint","IMPRINT",EDGE,{"disambiguationData":[TD([[subQ6,-1.0]])],"derivedFrom":subQ5}),1.0]])]});}
            var Q50;
            {var subQ0=sQuery(id+"F0.wireOp",EDGE,"E180");var subQ5=sQuery(id+"F0.wireOp",EDGE,"E179");var subQ6=makeQuery(id+"F0.imprint","INTERSECT",VERTEX,{"disambiguationData":[OD(1.0)],"derivedFrom":[subQ5,subQ0]});Q50=makeQuery(id+"F0.imprint","IMPRINT",FACE,{"disambiguationData":[TD([[makeQuery(id+"F0.imprint","IMPRINT",EDGE,{"disambiguationData":[TD([[subQ6,1.0]])],"derivedFrom":subQ5}),1.0]])]});}
            var Q51;
            {var subQ0=sQuery(id+"F0.wireOp",EDGE,"E180");var subQ5=sQuery(id+"F0.wireOp",EDGE,"E179");var subQ6=makeQuery(id+"F0.imprint","INTERSECT",VERTEX,{"disambiguationData":[OD(1.0)],"derivedFrom":[subQ5,subQ0]});Q51=makeQuery(id+"F0.imprint","IMPRINT",FACE,{"disambiguationData":[TD([[makeQuery(id+"F0.imprint","IMPRINT",EDGE,{"disambiguationData":[TD([[subQ6,1.0]])],"derivedFrom":subQ5}),-1.0]])]});}
            var Q52;
            {var subQ0=sQuery(id+"F0.wireOp",EDGE,"E180");var subQ5=sQuery(id+"F0.wireOp",EDGE,"E179");var subQ6=makeQuery(id+"F0.imprint","INTERSECT",VERTEX,{"disambiguationData":[OD(0.0)],"derivedFrom":[subQ5,subQ0]});Q52=makeQuery(id+"F0.imprint","IMPRINT",FACE,{"disambiguationData":[TD([[makeQuery(id+"F0.imprint","IMPRINT",EDGE,{"disambiguationData":[TD([[subQ6,-1.0]])],"derivedFrom":subQ5}),-1.0]])]});}
            var Q53;
            Q53=makeQuery(id+"F0.imprint","IMPRINT",FACE,{"disambiguationData":[TD([[makeQuery(id+"F0.imprint","IMPRINT",EDGE,{"derivedFrom":sQuery(id+"F0.wireOp",EDGE,"E160.MirrorC")}),-1.0]])]});
            var Q54;
            {var subQ1=sQuery(id+"F0.wireOp",EDGE,"E24");Q54=makeQuery(id+"F0.imprint","IMPRINT",FACE,{"disambiguationData":[TD([[makeQuery(id+"F0.imprint","IMPRINT",EDGE,{"derivedFrom":subQ1}),-1.0]])]});}
            var Q55;
            Q55=makeQuery(id+"F0.imprint","IMPRINT",FACE,{"disambiguationData":[TD([[makeQuery(id+"F0.imprint","IMPRINT",EDGE,{"derivedFrom":sQuery(id+"F0.wireOp",EDGE,"E19")}),1.0]])]});
            var Q56;
            {var subQ0=sQuery(id+"F0.wireOp",EDGE,"E209.MirrorCS");Q56=makeQuery(id+"F0.imprint","IMPRINT",FACE,{"disambiguationData":[TD([[makeQuery(id+"F0.imprint","IMPRINT",EDGE,{"derivedFrom":subQ0}),-1.0]])]});}
            var Q57;
            {var subQ0=sQuery(id+"F0.wireOp",EDGE,"E211.MirrorCS");Q57=makeQuery(id+"F0.imprint","IMPRINT",FACE,{"disambiguationData":[TD([[makeQuery(id+"F0.imprint","IMPRINT",EDGE,{"derivedFrom":subQ0}),1.0]])]});}
            var Q58;
            {var subQ2=sQuery(id+"F0.wireOp",EDGE,"E214.MirrorCS");Q58=makeQuery(id+"F0.imprint","IMPRINT",FACE,{"disambiguationData":[TD([[makeQuery(id+"F0.imprint","IMPRINT",EDGE,{"derivedFrom":subQ2}),1.0]])]});}
            var Q59;
            Q59=makeQuery(id+"F0.imprint","IMPRINT",FACE,{"disambiguationData":[TD([[makeQuery(id+"F0.imprint","IMPRINT",EDGE,{"derivedFrom":sQuery(id+"F0.wireOp",EDGE,"E123.MirrorCS")}),-1.0]])]});
            var Q60;
            Q60=makeQuery(id+"F0.imprint","IMPRINT",FACE,{"disambiguationData":[TD([[makeQuery(id+"F0.imprint","IMPRINT",EDGE,{"derivedFrom":sQuery(id+"F0.wireOp",EDGE,"E109.MirrorCS")}),1.0]])]});
            var Q61;
            Q61=makeQuery(id+"F0.imprint","IMPRINT",FACE,{"disambiguationData":[TD([[makeQuery(id+"F0.imprint","IMPRINT",EDGE,{"derivedFrom":sQuery(id+"F0.wireOp",EDGE,"E5")}),-1.0]])]});
            extrude(context, id + "F1", {"entities" : qUnion([Q0, Q1, Q2, Q3, Q4, Q5, Q6, Q7, Q8, Q9, Q10, Q11, Q12, Q13, Q14, Q15, Q16, Q17, Q18, Q19, Q20, Q21, Q22, Q23, Q24, Q25, Q26, Q27, Q28, Q29, Q30, Q31, Q32, Q33, Q34, Q35, Q36, Q37, Q38, Q39, Q40, Q41, Q42, Q43, Q44, Q45, Q46, Q47, Q48, Q49, Q50, Q51, Q52, Q53, Q54, Q55, Q56, Q57, Q58, Q59, Q60, Q61]), "depth" : 12.7 * mm});
        }
        {
            var Q0;
            Q0=makeQuery(id+"F0.imprint","IMPRINT",FACE,{"disambiguationData":[TD([[makeQuery(id+"F0.imprint","IMPRINT",EDGE,{"derivedFrom":sQuery(id+"F0.wireOp",EDGE,"E5")}),1.0]])]});
            var Q1;
            {var subQ1=sQuery(id+"F0.wireOp",EDGE,"E20");Q1=makeQuery(id+"F0.imprint","IMPRINT",FACE,{"disambiguationData":[TD([[makeQuery(id+"F0.imprint","IMPRINT",EDGE,{"derivedFrom":subQ1}),-1.0]])]});}
            var Q2;
            {var subQ2=sQuery(id+"F0.wireOp",EDGE,"E25");Q2=makeQuery(id+"F0.imprint","IMPRINT",FACE,{"disambiguationData":[TD([[makeQuery(id+"F0.imprint","IMPRINT",EDGE,{"derivedFrom":subQ2}),-1.0]])]});}
            var Q3;
            {var subQ0=sQuery(id+"F0.wireOp",EDGE,"E70");Q3=makeQuery(id+"F0.imprint","IMPRINT",FACE,{"disambiguationData":[TD([[makeQuery(id+"F0.imprint","IMPRINT",EDGE,{"derivedFrom":subQ0}),-1.0]])]});}
            var Q4;
            {var subQ4=sQuery(id+"F0.wireOp",EDGE,"E76");Q4=makeQuery(id+"F0.imprint","IMPRINT",FACE,{"disambiguationData":[TD([[makeQuery(id+"F0.imprint","IMPRINT",EDGE,{"derivedFrom":subQ4}),-1.0]])]});}
            var Q5;
            {var subQ0=sQuery(id+"F0.wireOp",EDGE,"E74");Q5=makeQuery(id+"F0.imprint","IMPRINT",FACE,{"disambiguationData":[TD([[makeQuery(id+"F0.imprint","IMPRINT",EDGE,{"derivedFrom":subQ0}),-1.0]])]});}
            var Q6;
            {var subQ4=sQuery(id+"F0.wireOp",EDGE,"E72");Q6=makeQuery(id+"F0.imprint","IMPRINT",FACE,{"disambiguationData":[TD([[makeQuery(id+"F0.imprint","IMPRINT",EDGE,{"derivedFrom":subQ4}),-1.0]])]});}
            var Q7;
            {var subQ0=sQuery(id+"F0.wireOp",EDGE,"E89.MirrorCS");Q7=makeQuery(id+"F0.imprint","IMPRINT",FACE,{"disambiguationData":[TD([[makeQuery(id+"F0.imprint","IMPRINT",EDGE,{"derivedFrom":subQ0}),-1.0]])]});}
            var Q8;
            {var subQ0=sQuery(id+"F0.wireOp",EDGE,"E83");Q8=makeQuery(id+"F0.imprint","IMPRINT",FACE,{"disambiguationData":[TD([[makeQuery(id+"F0.imprint","IMPRINT",EDGE,{"derivedFrom":subQ0}),1.0]])]});}
            var Q9;
            {var subQ0=sQuery(id+"F0.wireOp",EDGE,"E85");Q9=makeQuery(id+"F0.imprint","IMPRINT",FACE,{"disambiguationData":[TD([[makeQuery(id+"F0.imprint","IMPRINT",EDGE,{"derivedFrom":subQ0}),-1.0]])]});}
            var Q10;
            {var subQ4=sQuery(id+"F0.wireOp",EDGE,"E87.MirrorCS");Q10=makeQuery(id+"F0.imprint","IMPRINT",FACE,{"disambiguationData":[TD([[makeQuery(id+"F0.imprint","IMPRINT",EDGE,{"derivedFrom":subQ4}),1.0]])]});}
            var Q11;
            Q11=makeQuery(id+"F0.imprint","IMPRINT",FACE,{"disambiguationData":[TD([[makeQuery(id+"F0.imprint","IMPRINT",EDGE,{"derivedFrom":sQuery(id+"F0.wireOp",EDGE,"E93.MirrorCS")}),1.0]])]});
            var Q12;
            {var subQ4=sQuery(id+"F0.wireOp",EDGE,"E195");Q12=makeQuery(id+"F0.imprint","IMPRINT",FACE,{"disambiguationData":[TD([[makeQuery(id+"F0.imprint","IMPRINT",EDGE,{"derivedFrom":subQ4}),1.0]])]});}
            var Q13;
            {var subQ0=sQuery(id+"F0.wireOp",EDGE,"E179");var subQ1=sQuery(id+"F0.wireOp",EDGE,"E178");var subQ2=makeQuery(id+"F0.imprint","INTERSECT",VERTEX,{"derivedFrom":[subQ1,subQ0]});Q13=makeQuery(id+"F0.imprint","IMPRINT",FACE,{"disambiguationData":[TD([[makeQuery(id+"F0.imprint","IMPRINT",EDGE,{"disambiguationData":[TD([[subQ2,-1.0]])],"derivedFrom":subQ1}),-1.0]])]});}
            var Q14;
            {var subQ0=sQuery(id+"F0.wireOp",EDGE,"E179");var subQ1=sQuery(id+"F0.wireOp",EDGE,"E178");var subQ2=makeQuery(id+"F0.imprint","INTERSECT",VERTEX,{"derivedFrom":[subQ1,subQ0]});Q14=makeQuery(id+"F0.imprint","IMPRINT",FACE,{"disambiguationData":[TD([[makeQuery(id+"F0.imprint","IMPRINT",EDGE,{"disambiguationData":[TD([[subQ2,-1.0]])],"derivedFrom":subQ1}),1.0]])]});}
            var Q15;
            {var subQ0=sQuery(id+"F0.wireOp",EDGE,"E181");var subQ1=sQuery(id+"F0.wireOp",EDGE,"E178");var subQ2=makeQuery(id+"F0.imprint","INTERSECT",VERTEX,{"disambiguationData":[OD(0.0)],"derivedFrom":[subQ1,subQ0]});Q15=makeQuery(id+"F0.imprint","IMPRINT",FACE,{"disambiguationData":[TD([[makeQuery(id+"F0.imprint","IMPRINT",EDGE,{"disambiguationData":[TD([[subQ2,-1.0]])],"derivedFrom":subQ1}),1.0]])]});}
            var Q16;
            {var subQ0=sQuery(id+"F0.wireOp",EDGE,"E181");var subQ1=sQuery(id+"F0.wireOp",EDGE,"E178");var subQ2=makeQuery(id+"F0.imprint","INTERSECT",VERTEX,{"disambiguationData":[OD(0.0)],"derivedFrom":[subQ1,subQ0]});Q16=makeQuery(id+"F0.imprint","IMPRINT",FACE,{"disambiguationData":[TD([[makeQuery(id+"F0.imprint","IMPRINT",EDGE,{"disambiguationData":[TD([[subQ2,-1.0]])],"derivedFrom":subQ1}),-1.0]])]});}
            var Q17;
            {var subQ0=sQuery(id+"F0.wireOp",EDGE,"E170");Q17=makeQuery(id+"F0.imprint","IMPRINT",FACE,{"disambiguationData":[TD([[makeQuery(id+"F0.imprint","IMPRINT",EDGE,{"derivedFrom":subQ0}),1.0]])]});}
            var Q18;
            {var subQ0=sQuery(id+"F0.wireOp",EDGE,"E162");Q18=makeQuery(id+"F0.imprint","IMPRINT",FACE,{"disambiguationData":[TD([[makeQuery(id+"F0.imprint","IMPRINT",EDGE,{"derivedFrom":subQ0}),1.0]])]});}
            var Q19;
            {var subQ0=sQuery(id+"F0.wireOp",EDGE,"E161");Q19=makeQuery(id+"F0.imprint","IMPRINT",FACE,{"disambiguationData":[TD([[makeQuery(id+"F0.imprint","IMPRINT",EDGE,{"derivedFrom":subQ0}),-1.0]])]});}
            var Q20;
            {var subQ0=sQuery(id+"F0.wireOp",EDGE,"E172");Q20=makeQuery(id+"F0.imprint","IMPRINT",FACE,{"disambiguationData":[TD([[makeQuery(id+"F0.imprint","IMPRINT",EDGE,{"derivedFrom":subQ0}),-1.0]])]});}
            var Q21;
            {var subQ0=sQuery(id+"F0.wireOp",EDGE,"E176");Q21=makeQuery(id+"F0.imprint","IMPRINT",FACE,{"disambiguationData":[TD([[makeQuery(id+"F0.imprint","IMPRINT",EDGE,{"derivedFrom":subQ0}),-1.0]])]});}
            var Q22;
            {var subQ0=sQuery(id+"F0.wireOp",EDGE,"E174");Q22=makeQuery(id+"F0.imprint","IMPRINT",FACE,{"disambiguationData":[TD([[makeQuery(id+"F0.imprint","IMPRINT",EDGE,{"derivedFrom":subQ0}),-1.0]])]});}
            var Q23;
            {var subQ0=sQuery(id+"F0.wireOp",EDGE,"E188");var subQ1=sQuery(id+"F0.wireOp",EDGE,"E186");var subQ2=makeQuery(id+"F0.imprint","INTERSECT",VERTEX,{"disambiguationData":[OD(0.0)],"derivedFrom":[subQ1,subQ0]});Q23=makeQuery(id+"F0.imprint","IMPRINT",FACE,{"disambiguationData":[TD([[makeQuery(id+"F0.imprint","IMPRINT",EDGE,{"disambiguationData":[TD([[subQ2,-1.0]])],"derivedFrom":subQ1}),1.0]])]});}
            var Q24;
            {var subQ0=sQuery(id+"F0.wireOp",EDGE,"E188");var subQ1=sQuery(id+"F0.wireOp",EDGE,"E186");var subQ2=makeQuery(id+"F0.imprint","INTERSECT",VERTEX,{"disambiguationData":[OD(0.0)],"derivedFrom":[subQ1,subQ0]});Q24=makeQuery(id+"F0.imprint","IMPRINT",FACE,{"disambiguationData":[TD([[makeQuery(id+"F0.imprint","IMPRINT",EDGE,{"disambiguationData":[TD([[subQ2,-1.0]])],"derivedFrom":subQ1}),-1.0]])]});}
            var Q25;
            {var subQ0=sQuery(id+"F0.wireOp",EDGE,"E190");var subQ4=makeQuery(id+"F0.imprint","INTERSECT",VERTEX,{"derivedFrom":[subQ0,sQuery(id+"F0.wireOp",EDGE,"E192")]});Q25=makeQuery(id+"F0.imprint","IMPRINT",FACE,{"disambiguationData":[TD([[makeQuery(id+"F0.imprint","IMPRINT",EDGE,{"disambiguationData":[TD([[subQ4,1.0]])],"derivedFrom":subQ0}),-1.0]])]});}
            var Q26;
            {var subQ3=sQuery(id+"F0.wireOp",EDGE,"E193");Q26=makeQuery(id+"F0.imprint","IMPRINT",FACE,{"disambiguationData":[TD([[makeQuery(id+"F0.imprint","IMPRINT",EDGE,{"derivedFrom":subQ3}),-1.0]])]});}
            var Q27;
            {var subQ0=sQuery(id+"F0.wireOp",EDGE,"E192");var subQ1=sQuery(id+"F0.wireOp",EDGE,"E189");var subQ2=makeQuery(id+"F0.imprint","INTERSECT",VERTEX,{"derivedFrom":[subQ1,subQ0]});Q27=makeQuery(id+"F0.imprint","IMPRINT",FACE,{"disambiguationData":[TD([[makeQuery(id+"F0.imprint","IMPRINT",EDGE,{"disambiguationData":[TD([[subQ2,-1.0]])],"derivedFrom":subQ1}),1.0]])]});}
            var Q28;
            {var subQ0=sQuery(id+"F0.wireOp",EDGE,"E191");var subQ1=sQuery(id+"F0.wireOp",EDGE,"E189");var subQ2=makeQuery(id+"F0.imprint","INTERSECT",VERTEX,{"disambiguationData":[OD(0.0)],"derivedFrom":[subQ1,subQ0]});Q28=makeQuery(id+"F0.imprint","IMPRINT",FACE,{"disambiguationData":[TD([[makeQuery(id+"F0.imprint","IMPRINT",EDGE,{"disambiguationData":[TD([[subQ2,-1.0]])],"derivedFrom":subQ1}),1.0]])]});}
            var Q29;
            {var subQ0=sQuery(id+"F0.wireOp",EDGE,"E191");var subQ1=sQuery(id+"F0.wireOp",EDGE,"E189");var subQ2=makeQuery(id+"F0.imprint","INTERSECT",VERTEX,{"disambiguationData":[OD(0.0)],"derivedFrom":[subQ1,subQ0]});Q29=makeQuery(id+"F0.imprint","IMPRINT",FACE,{"disambiguationData":[TD([[makeQuery(id+"F0.imprint","IMPRINT",EDGE,{"disambiguationData":[TD([[subQ2,-1.0]])],"derivedFrom":subQ1}),-1.0]])]});}
            var Q30;
            {var subQ0=sQuery(id+"F0.wireOp",EDGE,"E192");var subQ1=sQuery(id+"F0.wireOp",EDGE,"E189");var subQ2=makeQuery(id+"F0.imprint","INTERSECT",VERTEX,{"derivedFrom":[subQ1,subQ0]});Q30=makeQuery(id+"F0.imprint","IMPRINT",FACE,{"disambiguationData":[TD([[makeQuery(id+"F0.imprint","IMPRINT",EDGE,{"disambiguationData":[TD([[subQ2,-1.0]])],"derivedFrom":subQ1}),-1.0]])]});}
            var Q31;
            {var subQ0=sQuery(id+"F0.wireOp",EDGE,"E146");Q31=makeQuery(id+"F0.imprint","IMPRINT",FACE,{"disambiguationData":[TD([[makeQuery(id+"F0.imprint","IMPRINT",EDGE,{"derivedFrom":subQ0}),1.0]])]});}
            var Q32;
            {var subQ0=sQuery(id+"F0.wireOp",EDGE,"E148");Q32=makeQuery(id+"F0.imprint","IMPRINT",FACE,{"disambiguationData":[TD([[makeQuery(id+"F0.imprint","IMPRINT",EDGE,{"derivedFrom":subQ0}),1.0]])]});}
            var Q33;
            {var subQ0=sQuery(id+"F0.wireOp",EDGE,"E150");Q33=makeQuery(id+"F0.imprint","IMPRINT",FACE,{"disambiguationData":[TD([[makeQuery(id+"F0.imprint","IMPRINT",EDGE,{"derivedFrom":subQ0}),1.0]])]});}
            var Q34;
            {var subQ0=sQuery(id+"F0.wireOp",EDGE,"E151");Q34=makeQuery(id+"F0.imprint","IMPRINT",FACE,{"disambiguationData":[TD([[makeQuery(id+"F0.imprint","IMPRINT",EDGE,{"derivedFrom":subQ0}),-1.0]])]});}
            var Q35;
            {var subQ0=sQuery(id+"F0.wireOp",EDGE,"E206");Q35=makeQuery(id+"F0.imprint","IMPRINT",FACE,{"disambiguationData":[TD([[makeQuery(id+"F0.imprint","IMPRINT",EDGE,{"derivedFrom":subQ0}),-1.0]])]});}
            var Q36;
            {var subQ3=sQuery(id+"F0.wireOp",EDGE,"E202");var subQ5=sQuery(id+"F0.wireOp",EDGE,"E203");var subQ6=makeQuery(id+"F0.imprint","INTERSECT",VERTEX,{"disambiguationData":[OD(0.0)],"derivedFrom":[subQ3,subQ5]});Q36=makeQuery(id+"F0.imprint","IMPRINT",FACE,{"disambiguationData":[TD([[makeQuery(id+"F0.imprint","IMPRINT",EDGE,{"disambiguationData":[TD([[subQ6,-1.0]])],"derivedFrom":subQ3}),1.0]])]});}
            var Q37;
            {var subQ3=sQuery(id+"F0.wireOp",EDGE,"E202");var subQ5=sQuery(id+"F0.wireOp",EDGE,"E203");var subQ7=makeQuery(id+"F0.imprint","INTERSECT",VERTEX,{"disambiguationData":[OD(0.0)],"derivedFrom":[subQ3,subQ5]});Q37=makeQuery(id+"F0.imprint","IMPRINT",FACE,{"disambiguationData":[TD([[makeQuery(id+"F0.imprint","IMPRINT",EDGE,{"disambiguationData":[TD([[subQ7,1.0]])],"derivedFrom":subQ3}),1.0]])]});}
            var Q38;
            {var subQ1=sQuery(id+"F0.wireOp",EDGE,"E200");var subQ3=sQuery(id+"F0.wireOp",EDGE,"E202");var subQ4=makeQuery(id+"F0.imprint","INTERSECT",VERTEX,{"disambiguationData":[OD(0.0)],"derivedFrom":[subQ1,subQ3]});Q38=makeQuery(id+"F0.imprint","IMPRINT",FACE,{"disambiguationData":[TD([[makeQuery(id+"F0.imprint","IMPRINT",EDGE,{"disambiguationData":[TD([[subQ4,1.0]])],"derivedFrom":subQ3}),1.0]])]});}
            var Q39;
            {var subQ0=sQuery(id+"F0.wireOp",EDGE,"E203");var subQ1=sQuery(id+"F0.wireOp",EDGE,"E202");var subQ2=makeQuery(id+"F0.imprint","INTERSECT",VERTEX,{"disambiguationData":[OD(1.0)],"derivedFrom":[subQ1,subQ0]});Q39=makeQuery(id+"F0.imprint","IMPRINT",FACE,{"disambiguationData":[TD([[makeQuery(id+"F0.imprint","IMPRINT",EDGE,{"disambiguationData":[TD([[subQ2,1.0]])],"derivedFrom":subQ1}),1.0]])]});}
            var Q40;
            {var subQ0=sQuery(id+"F0.wireOp",EDGE,"E203");var subQ1=sQuery(id+"F0.wireOp",EDGE,"E201");var subQ2=makeQuery(id+"F0.imprint","INTERSECT",VERTEX,{"derivedFrom":[subQ1,subQ0]});Q40=makeQuery(id+"F0.imprint","IMPRINT",FACE,{"disambiguationData":[TD([[makeQuery(id+"F0.imprint","IMPRINT",EDGE,{"disambiguationData":[TD([[subQ2,1.0]])],"derivedFrom":subQ1}),1.0]])]});}
            var Q41;
            {var subQ0=sQuery(id+"F0.wireOp",EDGE,"E154");Q41=makeQuery(id+"F0.imprint","IMPRINT",FACE,{"disambiguationData":[TD([[makeQuery(id+"F0.imprint","IMPRINT",EDGE,{"derivedFrom":subQ0}),-1.0]])]});}
            var Q42;
            {var subQ0=sQuery(id+"F0.wireOp",EDGE,"E185");var subQ1=sQuery(id+"F0.wireOp",EDGE,"E182");var subQ2=makeQuery(id+"F0.imprint","INTERSECT",VERTEX,{"disambiguationData":[OD(0.0)],"derivedFrom":[subQ1,subQ0]});Q42=makeQuery(id+"F0.imprint","IMPRINT",FACE,{"disambiguationData":[TD([[makeQuery(id+"F0.imprint","IMPRINT",EDGE,{"disambiguationData":[TD([[subQ2,-1.0]])],"derivedFrom":subQ1}),-1.0]])]});}
            var Q43;
            {var subQ0=sQuery(id+"F0.wireOp",EDGE,"E185");var subQ1=sQuery(id+"F0.wireOp",EDGE,"E182");var subQ2=makeQuery(id+"F0.imprint","INTERSECT",VERTEX,{"disambiguationData":[OD(0.0)],"derivedFrom":[subQ1,subQ0]});Q43=makeQuery(id+"F0.imprint","IMPRINT",FACE,{"disambiguationData":[TD([[makeQuery(id+"F0.imprint","IMPRINT",EDGE,{"disambiguationData":[TD([[subQ2,-1.0]])],"derivedFrom":subQ1}),1.0]])]});}
            var Q44;
            {var subQ0=sQuery(id+"F0.wireOp",EDGE,"E183");var subQ1=sQuery(id+"F0.wireOp",EDGE,"E182");var subQ2=makeQuery(id+"F0.imprint","INTERSECT",VERTEX,{"derivedFrom":[subQ1,subQ0]});Q44=makeQuery(id+"F0.imprint","IMPRINT",FACE,{"disambiguationData":[TD([[makeQuery(id+"F0.imprint","IMPRINT",EDGE,{"disambiguationData":[TD([[subQ2,-1.0]])],"derivedFrom":subQ1}),1.0]])]});}
            var Q45;
            {var subQ0=sQuery(id+"F0.wireOp",EDGE,"E183");var subQ1=sQuery(id+"F0.wireOp",EDGE,"E182");var subQ2=makeQuery(id+"F0.imprint","INTERSECT",VERTEX,{"derivedFrom":[subQ1,subQ0]});Q45=makeQuery(id+"F0.imprint","IMPRINT",FACE,{"disambiguationData":[TD([[makeQuery(id+"F0.imprint","IMPRINT",EDGE,{"disambiguationData":[TD([[subQ2,-1.0]])],"derivedFrom":subQ1}),-1.0]])]});}
            var Q46;
            {var subQ0=sQuery(id+"F0.wireOp",EDGE,"E152");Q46=makeQuery(id+"F0.imprint","IMPRINT",FACE,{"disambiguationData":[TD([[makeQuery(id+"F0.imprint","IMPRINT",EDGE,{"derivedFrom":subQ0}),1.0]])]});}
            var Q47;
            Q47=makeQuery(id+"F0.imprint","IMPRINT",FACE,{"disambiguationData":[TD([[makeQuery(id+"F0.imprint","IMPRINT",EDGE,{"derivedFrom":sQuery(id+"F0.wireOp",EDGE,"E196")}),1.0]])]});
            extrude(context, id + "F2", {"entities" : qUnion([Q0, Q1, Q2, Q3, Q4, Q5, Q6, Q7, Q8, Q9, Q10, Q11, Q12, Q13, Q14, Q15, Q16, Q17, Q18, Q19, Q20, Q21, Q22, Q23, Q24, Q25, Q26, Q27, Q28, Q29, Q30, Q31, Q32, Q33, Q34, Q35, Q36, Q37, Q38, Q39, Q40, Q41, Q42, Q43, Q44, Q45, Q46, Q47]), "depth" : 10.8 * mm});
        }
    });
